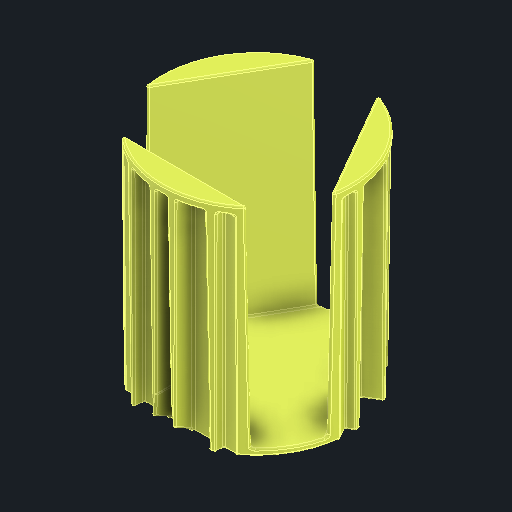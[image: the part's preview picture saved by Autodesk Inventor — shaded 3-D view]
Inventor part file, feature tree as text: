
AUTODESK INVENTOR PART (.ipt)
format: ipt  version: 2024.2 (Build 282272000, 272)  size: 865,280 bytes
history: native  units: in
note: dims shown in document units (in); Inventor stores cm internally (conversion verified against a paired STEP export)
features: fillet x1
ambient origin geometry x8: Origin, YZ Plane, XZ Plane, XY Plane, X Axis, Y Axis, Z Axis, Center Point
bodies: Solid1 (feature_tree)
feature tree (1):
  fillet  "Fillet21"  [1 undecoded]
note: 1 required parameter value undecoded (feature->parameter linkage not recoverable at this tier; creation-order binding heuristic only, values carry confidence <= 0.55)
